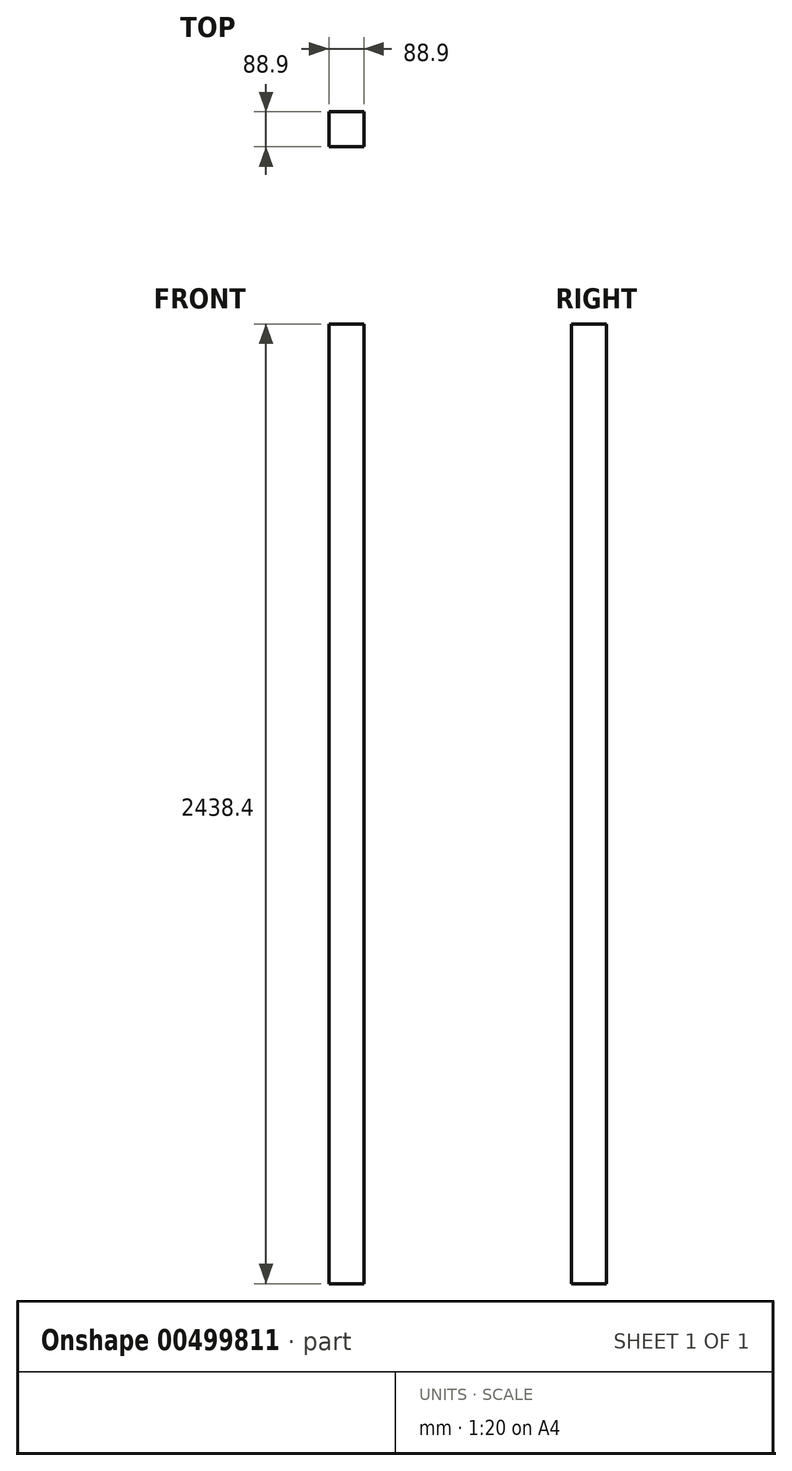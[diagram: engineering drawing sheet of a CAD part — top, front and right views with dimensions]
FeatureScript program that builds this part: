
annotation { "Feature Type Name" : "Feature", "Feature Type Description" : "" }
export const myFeature = defineFeature(function(context is Context, id is Id, definition is map)
    precondition{}
    {
        {
            var Q0;
            Q0=qCreatedBy(makeId("Front.planeOp"),FACE);
            var sketch = newSketch(context, id + "F0", { "sketchPlane" : qUnion([Q0])});
            skLineSegment(sketch, "E0.bottom", {"start": v(-44.45, -1219.2) * mm, "end": v(44.45, -1219.2) * mm});
            skLineSegment(sketch, "E0.top", {"start": v(-44.45, 1219.2) * mm, "end": v(44.45, 1219.2) * mm});
            skLineSegment(sketch, "E0.left", {"start": v(-44.45, -1219.2) * mm, "end": v(-44.45, 1219.2) * mm});
            skLineSegment(sketch, "E0.right", {"start": v(44.45, -1219.2) * mm, "end": v(44.45, 1219.2) * mm});
            skPoint(sketch, "E0.middle", {"position": v(0, 0) * mm});
            skSolve(sketch);
        }
        {
            var Q0;
            Q0 = qSketchRegion(id + "F0", true);
            extrude(context, id + "F1", {"entities" : qUnion([Q0]), "depth" : 88.9 * mm});
        }
    });
